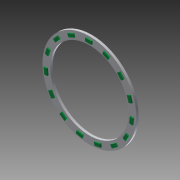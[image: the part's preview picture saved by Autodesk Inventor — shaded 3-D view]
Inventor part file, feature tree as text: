
AUTODESK INVENTOR PART (.ipt)
format: ipt  version: 2016 SP1 (Build 200210100, 210)  size: 151,040 bytes
history: native  units: mm
features: extrude x2, sketch x2, pattern_circular x1
ambient origin geometry x8: Origin, YZ Plane, XZ Plane, XY Plane, X Axis, Y Axis, Z Axis, Center Point
bodies: Solid1 (feature_tree)
feature tree (5):
  extrude  "Extrusion1"  Depth=50.0mm
  extrude  "Extrusion2"  Depth=2.0mm
  pattern_circular  "Circular Pattern1"  [2 undecoded]
  sketch  "Sketch1"  dims[d0=60.0mm d1=50.0mm]
  sketch  "Sketch2"  dims[d2=1.5mm d3=0.0mm d4=2.0mm d5=26.5mm d6=4.0mm d7=0.75mm d8=0.0mm d9=150.0mm d10=360.0deg]
note: 2 required parameter values undecoded (feature->parameter linkage not recoverable at this tier; creation-order binding heuristic only, values carry confidence <= 0.55)
